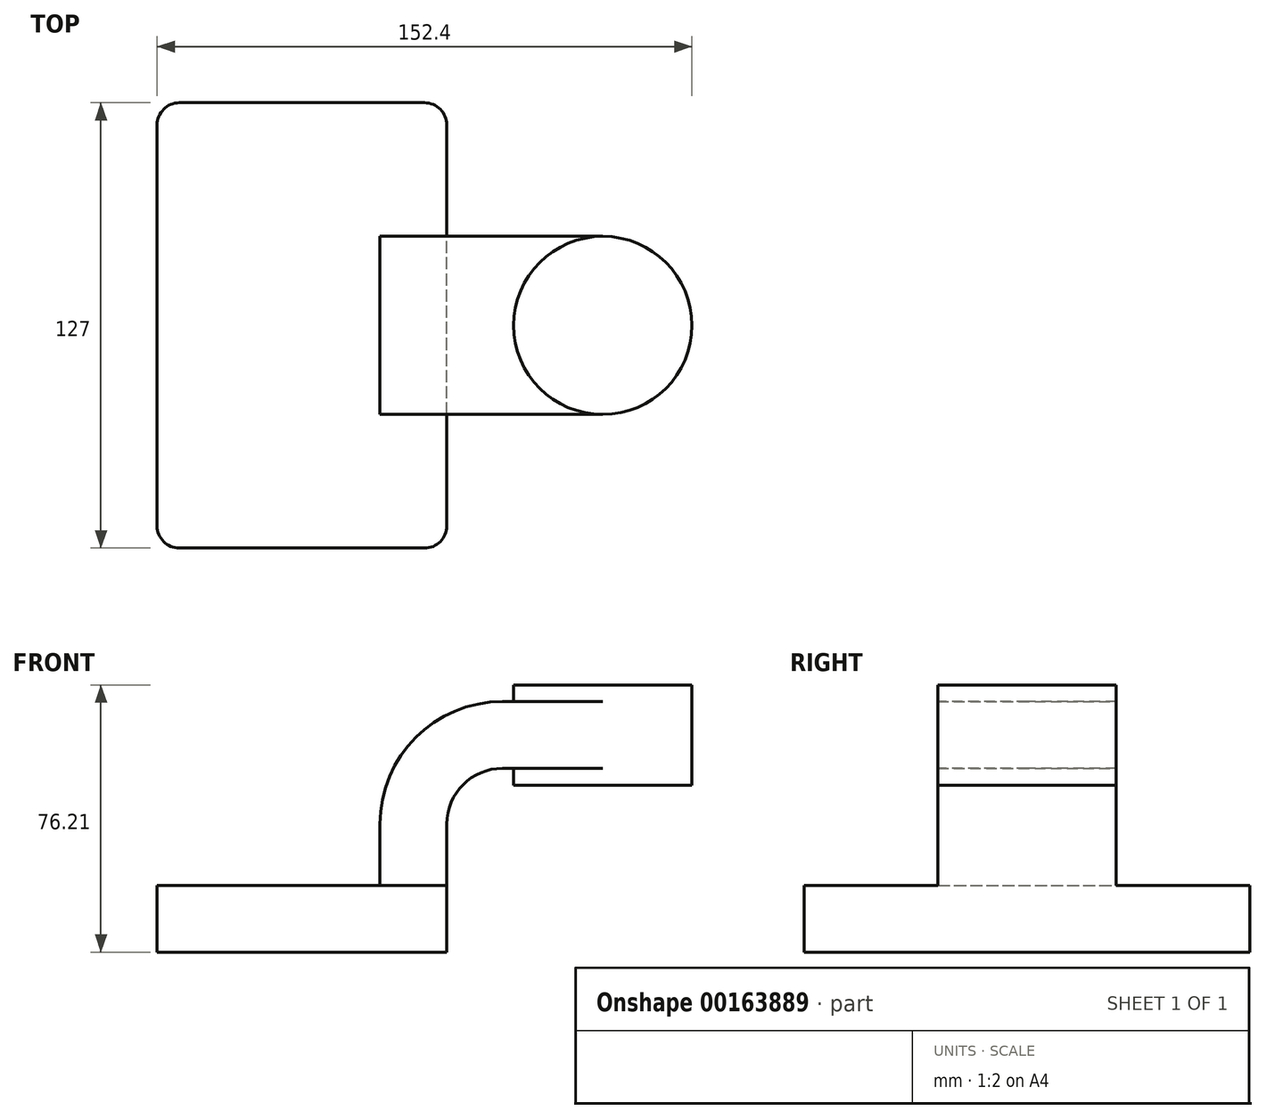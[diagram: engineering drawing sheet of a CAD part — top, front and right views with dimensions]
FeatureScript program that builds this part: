
annotation { "Feature Type Name" : "Feature", "Feature Type Description" : "" }
export const myFeature = defineFeature(function(context is Context, id is Id, definition is map)
    precondition{}
    {
        {
            var Q0;
            Q0=qCreatedBy(makeId("Front.planeOp"),FACE);
            var sketch = newSketch(context, id + "F0", { "sketchPlane" : qUnion([Q0])});
            skLineSegment(sketch, "E0.bottom", {"start": v(-41.28, 9.52) * mm, "end": v(41.27, 9.53) * mm});
            skLineSegment(sketch, "E0.top", {"start": v(-41.28, -9.53) * mm, "end": v(41.28, -9.53) * mm});
            skLineSegment(sketch, "E0.left", {"start": v(-41.28, 9.52) * mm, "end": v(-41.28, -9.53) * mm});
            skLineSegment(sketch, "E0.right", {"start": v(41.27, 9.53) * mm, "end": v(41.27, -9.52) * mm});
            skPoint(sketch, "E0.middle", {"position": v(0, 0) * mm});
            skLineSegment(sketch, "E1.bottom", {"start": v(111.12, 38.1) * mm, "end": v(60.32, 38.1) * mm});
            skLineSegment(sketch, "E1.top", {"start": v(111.12, 66.68) * mm, "end": v(60.32, 66.68) * mm});
            skLineSegment(sketch, "E1.left", {"start": v(111.12, 38.1) * mm, "end": v(111.12, 66.68) * mm});
            skLineSegment(sketch, "E1.right", {"start": v(60.32, 38.1) * mm, "end": v(60.32, 66.68) * mm});
            skPoint(sketch, "E1.middle", {"position": v(85.72, 52.39) * mm});
            skLineSegment(sketch, "E2", {"start": v(41.28, 9.53) * mm, "end": v(41.28, 27) * mm});
            skArc(sketch, "E3", {"start": v(41.27, 27) * mm, "mid": v(45.92, 38.23) * mm, "end": v(57.15, 42.88) * mm});
            skLineSegment(sketch, "E4", {"start": v(57.15, 42.88) * mm, "end": v(85.72, 42.88) * mm});
            skLineSegment(sketch, "E5.0", {"start": v(57.15, 61.93) * mm, "end": v(85.72, 61.93) * mm});
            skArc(sketch, "E5.1", {"start": v(22.23, 27) * mm, "mid": v(32.45, 51.7) * mm, "end": v(57.15, 61.93) * mm});
            skLineSegment(sketch, "E5.2", {"start": v(22.23, 9.53) * mm, "end": v(22.23, 27) * mm});
            skLineSegment(sketch, "E6", {"start": v(85.72, 38.1) * mm, "end": v(85.72, 66.68) * mm});
            skPoint(sketch, "E6.startSnap0", {"position": v(85.72, 38.1) * mm});
            skFitSpline(sketch, "E7", {"points": [v(-41.28, 9.52) * mm, v(57.15, 61.93) * mm], "startDerivative": vector(0.68, 89.53) * mm, "endDerivative": vector(135.03, 0) * mm});
            skSolve(sketch);
        }
        {
            var Q0;
            Q0=makeQuery(id+"F0.imprint","IMPRINT",FACE,{"disambiguationData":[TD([[makeQuery(id+"F0.imprint","IMPRINT",EDGE,{"derivedFrom":sQuery(id+"F0.wireOp",EDGE,"E0.top")}),1.0]])]});
            extrude(context, id + "F1", {"entities" : qUnion([Q0]), "endBound" : BoundingType.SYMMETRIC, "depth" : 127 * mm});
        }
        {
            var Q0;
            {var subQ1=sQuery(id+"F0.wireOp",EDGE,"E2");Q0=makeQuery(id+"F0.imprint","IMPRINT",FACE,{"disambiguationData":[TD([[makeQuery(id+"F0.imprint","IMPRINT",EDGE,{"derivedFrom":subQ1}),1.0]])]});}
            var Q1;
            {var subQ0=sQuery(id+"F0.wireOp",EDGE,"E4");var subQ1=sQuery(id+"F0.wireOp",EDGE,"E1.right");var subQ2=makeQuery(id+"F0.imprint","INTERSECT",VERTEX,{"derivedFrom":[subQ1,subQ0]});Q1=makeQuery(id+"F0.imprint","IMPRINT",FACE,{"disambiguationData":[TD([[makeQuery(id+"F0.imprint","IMPRINT",EDGE,{"disambiguationData":[TD([[subQ2,-1.0]])],"derivedFrom":subQ1}),-1.0]])]});}
            extrude(context, id + "F2", {"entities" : qUnion([Q0, Q1]), "operationType" : NewBodyOperationType.ADD, "endBound" : BoundingType.SYMMETRIC, "depth" : 50.8 * mm});
        }
        {
            var Q0;
            Q0=makeQuery(id+"F0.imprint","IMPRINT",FACE,{"disambiguationData":[TD([[makeQuery(id+"F0.imprint","IMPRINT",EDGE,{"derivedFrom":sQuery(id+"F0.wireOp",EDGE,"E5.1")}),1.0]])]});
            extrude(context, id + "F3", {"entities" : qUnion([Q0]), "operationType" : NewBodyOperationType.ADD, "endBound" : BoundingType.SYMMETRIC, "depth" : 15.88 * mm});
        }
        {
            var Q0;
            {var subQ0=sQuery(id+"F0.wireOp",EDGE,"E1.left");Q0=makeQuery(id+"F0.imprint","IMPRINT",FACE,{"disambiguationData":[TD([[makeQuery(id+"F0.imprint","IMPRINT",EDGE,{"derivedFrom":subQ0}),1.0]])]});}
            var Q1;
            Q1=sQuery(id+"F0.wireOp",EDGE,"E6");
            revolve(context, id + "F4", {"operationType" : NewBodyOperationType.ADD, "entities" : qUnion([Q0]), "axis" : qUnion([Q1]), "revolveType" : RevolveType.FULL});
        }
        {
            var Q0;
            Q0=makeQuery(id+"F1.opExtrude","CAP_EDGE",EDGE,{"disambiguationData":[OSD([sQuery(id+"F0.wireOp",EDGE,"E0.right")])],"isStart":true});
            var Q1;
            Q1=makeQuery(id+"F1.opExtrude","CAP_EDGE",EDGE,{"disambiguationData":[OSD([sQuery(id+"F0.wireOp",EDGE,"E0.left")])],"isStart":true});
            var Q2;
            Q2=makeQuery(id+"F1.opExtrude","CAP_EDGE",EDGE,{"disambiguationData":[OSD([sQuery(id+"F0.wireOp",EDGE,"E0.right")])],"isStart":false});
            var Q3;
            Q3=makeQuery(id+"F1.opExtrude","CAP_EDGE",EDGE,{"disambiguationData":[OSD([sQuery(id+"F0.wireOp",EDGE,"E0.left")])],"isStart":false});
            fillet(context, id + "F5", {"entities" : qUnion([Q0, Q1, Q2, Q3]), "radius" : 6.35 * mm, "tangentPropagation" : true, "allowEdgeOverflow" : false});
        }
    });
